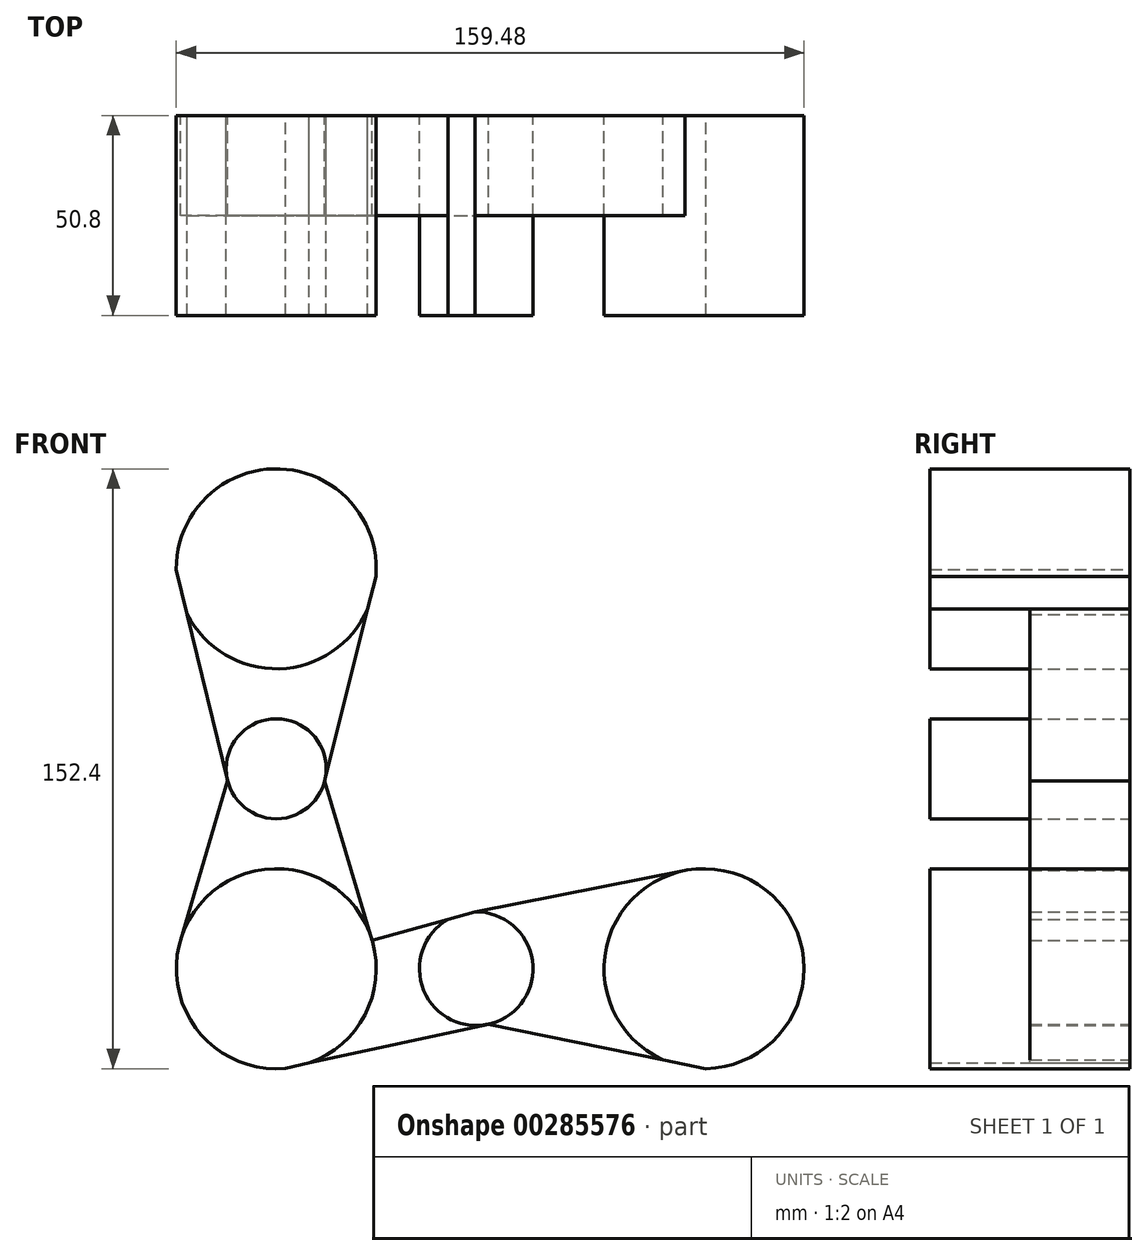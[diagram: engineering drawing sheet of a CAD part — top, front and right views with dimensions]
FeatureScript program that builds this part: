
annotation { "Feature Type Name" : "Feature", "Feature Type Description" : "" }
export const myFeature = defineFeature(function(context is Context, id is Id, definition is map)
    precondition{}
    {
        {
            var Q0;
            Q0=qCreatedBy(makeId("Front.planeOp"),FACE);
            var sketch = newSketch(context, id + "F0", { "sketchPlane" : qUnion([Q0])});
            skLineSegment(sketch, "E0", {"start": v(-135.65, -73.57) * mm, "end": v(-84.85, -73.57) * mm});
            skLineSegment(sketch, "E1", {"start": v(-77.77, -73.57) * mm, "end": v(-26.97, -73.57) * mm});
            skLineSegment(sketch, "E2", {"start": v(-135.65, -73.57) * mm, "end": v(-135.65, -22.77) * mm});
            skLineSegment(sketch, "E3", {"start": v(-135.65, -22.77) * mm, "end": v(-135.65, 28.03) * mm});
            skLineSegment(sketch, "E4", {"start": v(-77.77, -73.57) * mm, "end": v(-84.85, -73.57) * mm});
            skCircle(sketch, "E5", {"center": v(-135.65, 28.03) * mm, "radius": 25.4 * mm});
            skCircle(sketch, "E6", {"center": v(-135.65, -73.57) * mm, "radius": 25.4 * mm});
            skCircle(sketch, "E7", {"center": v(-26.97, -73.57) * mm, "radius": 25.4 * mm});
            skCircle(sketch, "E8", {"center": v(-84.85, -73.57) * mm, "radius": 14.43 * mm});
            skCircle(sketch, "E9", {"center": v(-135.65, -22.77) * mm, "radius": 12.7 * mm});
            skLineSegment(sketch, "E10", {"start": v(-161.05, 27.9) * mm, "end": v(-147.99, -25.77) * mm});
            skLineSegment(sketch, "E11", {"start": v(-147.99, -25.77) * mm, "end": v(-160, -66.36) * mm});
            skLineSegment(sketch, "E12", {"start": v(-110.32, 26.07) * mm, "end": v(-123.33, -25.85) * mm});
            skLineSegment(sketch, "E13", {"start": v(-123.33, -25.85) * mm, "end": v(-111.3, -66.33) * mm});
            skLineSegment(sketch, "E14", {"start": v(-133.3, -98.86) * mm, "end": v(-81.78, -87.67) * mm});
            skLineSegment(sketch, "E15", {"start": v(-81.78, -87.67) * mm, "end": v(-26.43, -98.96) * mm});
            skLineSegment(sketch, "E16", {"start": v(-111.3, -66.33) * mm, "end": v(-85.14, -59.14) * mm});
            skLineSegment(sketch, "E17", {"start": v(-85.14, -59.14) * mm, "end": v(-31.88, -48.65) * mm});
            skSolve(sketch);
        }
        {
            var Q0;
            {var subQ1=sQuery(id+"F0.wireOp",EDGE,"E5");var subQ4=makeQuery(id+"F0.imprint","INTERSECT",VERTEX,{"derivedFrom":[sQuery(id+"F0.wireOp",EDGE,"E3"),subQ1]});Q0=makeQuery(id+"F0.imprint","IMPRINT",FACE,{"disambiguationData":[TD([[makeQuery(id+"F0.imprint","IMPRINT",EDGE,{"disambiguationData":[TD([[subQ4,1.0]])],"derivedFrom":subQ1}),1.0]])]});}
            var Q1;
            {var subQ0=sQuery(id+"F0.wireOp",EDGE,"E3");var subQ1=sQuery(id+"F0.wireOp",EDGE,"E2");var subQ2=makeQuery(id+"F0.imprint","INTERSECT",VERTEX,{"derivedFrom":[subQ1,subQ0]});Q1=makeQuery(id+"F0.imprint","IMPRINT",FACE,{"disambiguationData":[TD([[makeQuery(id+"F0.imprint","IMPRINT",EDGE,{"disambiguationData":[TD([[subQ2,1.0]])],"derivedFrom":subQ1}),-1.0]])]});}
            var Q2;
            {var subQ0=sQuery(id+"F0.wireOp",EDGE,"E3");var subQ1=sQuery(id+"F0.wireOp",EDGE,"E2");var subQ2=makeQuery(id+"F0.imprint","INTERSECT",VERTEX,{"derivedFrom":[subQ1,subQ0]});Q2=makeQuery(id+"F0.imprint","IMPRINT",FACE,{"disambiguationData":[TD([[makeQuery(id+"F0.imprint","IMPRINT",EDGE,{"disambiguationData":[TD([[subQ2,1.0]])],"derivedFrom":subQ1}),1.0]])]});}
            var Q3;
            {var subQ5=sQuery(id+"F0.wireOp",EDGE,"E2");var subQ7=sQuery(id+"F0.wireOp",EDGE,"E0");var subQ8=makeQuery(id+"F0.imprint","INTERSECT",VERTEX,{"derivedFrom":[subQ7,subQ5]});Q3=makeQuery(id+"F0.imprint","IMPRINT",FACE,{"disambiguationData":[TD([[makeQuery(id+"F0.imprint","IMPRINT",EDGE,{"disambiguationData":[TD([[subQ8,-1.0]])],"derivedFrom":subQ7}),-1.0]])]});}
            var Q4;
            {var subQ4=sQuery(id+"F0.wireOp",EDGE,"E4");Q4=makeQuery(id+"F0.imprint","IMPRINT",FACE,{"disambiguationData":[TD([[makeQuery(id+"F0.imprint","IMPRINT",EDGE,{"derivedFrom":subQ4}),1.0]])]});}
            var Q5;
            {var subQ0=sQuery(id+"F0.wireOp",EDGE,"E7");var subQ1=makeQuery(id+"F0.imprint","INTERSECT",VERTEX,{"derivedFrom":[subQ0,sQuery(id+"F0.wireOp",EDGE,"E17")]});Q5=makeQuery(id+"F0.imprint","IMPRINT",FACE,{"disambiguationData":[TD([[makeQuery(id+"F0.imprint","IMPRINT",EDGE,{"disambiguationData":[TD([[subQ1,-1.0]])],"derivedFrom":subQ0}),1.0]])]});}
            var Q6;
            {var subQ0=sQuery(id+"F0.wireOp",EDGE,"E2");var subQ1=sQuery(id+"F0.wireOp",EDGE,"E0");var subQ2=makeQuery(id+"F0.imprint","INTERSECT",VERTEX,{"derivedFrom":[subQ1,subQ0]});Q6=makeQuery(id+"F0.imprint","IMPRINT",FACE,{"disambiguationData":[TD([[makeQuery(id+"F0.imprint","IMPRINT",EDGE,{"disambiguationData":[TD([[subQ2,-1.0]])],"derivedFrom":subQ1}),1.0]])]});}
            var Q7;
            {var subQ5=sQuery(id+"F0.wireOp",EDGE,"E4");Q7=makeQuery(id+"F0.imprint","IMPRINT",FACE,{"disambiguationData":[TD([[makeQuery(id+"F0.imprint","IMPRINT",EDGE,{"derivedFrom":subQ5}),-1.0]])]});}
            extrude(context, id + "F1", {"entities" : qUnion([Q0, Q1, Q2, Q3, Q4, Q5, Q6, Q7]), "depth" : 50.8 * mm});
        }
        {
            var Q0;
            {var subQ0=sQuery(id+"F0.wireOp",EDGE,"E5");var subQ1=sQuery(id+"F0.wireOp",EDGE,"E3");var subQ2=makeQuery(id+"F0.imprint","INTERSECT",VERTEX,{"derivedFrom":[subQ1,subQ0]});Q0=makeQuery(id+"F0.imprint","IMPRINT",FACE,{"disambiguationData":[TD([[makeQuery(id+"F0.imprint","IMPRINT",EDGE,{"disambiguationData":[TD([[subQ2,1.0]])],"derivedFrom":subQ1}),1.0]])]});}
            var Q1;
            {var subQ0=sQuery(id+"F0.wireOp",EDGE,"E5");var subQ1=sQuery(id+"F0.wireOp",EDGE,"E3");var subQ2=makeQuery(id+"F0.imprint","INTERSECT",VERTEX,{"derivedFrom":[subQ1,subQ0]});Q1=makeQuery(id+"F0.imprint","IMPRINT",FACE,{"disambiguationData":[TD([[makeQuery(id+"F0.imprint","IMPRINT",EDGE,{"disambiguationData":[TD([[subQ2,1.0]])],"derivedFrom":subQ1}),-1.0]])]});}
            var Q2;
            {var subQ5=sQuery(id+"F0.wireOp",EDGE,"E13");Q2=makeQuery(id+"F0.imprint","IMPRINT",FACE,{"disambiguationData":[TD([[makeQuery(id+"F0.imprint","IMPRINT",EDGE,{"derivedFrom":subQ5}),-1.0]])]});}
            var Q3;
            {var subQ5=sQuery(id+"F0.wireOp",EDGE,"E11");Q3=makeQuery(id+"F0.imprint","IMPRINT",FACE,{"disambiguationData":[TD([[makeQuery(id+"F0.imprint","IMPRINT",EDGE,{"derivedFrom":subQ5}),1.0]])]});}
            var Q4;
            {var subQ5=sQuery(id+"F0.wireOp",EDGE,"E17");Q4=makeQuery(id+"F0.imprint","IMPRINT",FACE,{"disambiguationData":[TD([[makeQuery(id+"F0.imprint","IMPRINT",EDGE,{"derivedFrom":subQ5}),-1.0]])]});}
            var Q5;
            {var subQ0=sQuery(id+"F0.wireOp",EDGE,"E7");var subQ1=sQuery(id+"F0.wireOp",EDGE,"E1");var subQ2=makeQuery(id+"F0.imprint","INTERSECT",VERTEX,{"derivedFrom":[subQ1,subQ0]});Q5=makeQuery(id+"F0.imprint","IMPRINT",FACE,{"disambiguationData":[TD([[makeQuery(id+"F0.imprint","IMPRINT",EDGE,{"disambiguationData":[TD([[subQ2,1.0]])],"derivedFrom":subQ1}),-1.0]])]});}
            extrude(context, id + "F2", {"entities" : qUnion([Q0, Q1, Q2, Q3, Q4, Q5]), "depth" : 25.4 * mm});
        }
        {
            var Q0;
            {var subQ0=sQuery(id+"F0.wireOp",EDGE,"E6");var subQ1=sQuery(id+"F0.wireOp",EDGE,"E0");var subQ2=makeQuery(id+"F0.imprint","INTERSECT",VERTEX,{"derivedFrom":[subQ1,subQ0]});Q0=makeQuery(id+"F0.imprint","IMPRINT",FACE,{"disambiguationData":[TD([[makeQuery(id+"F0.imprint","IMPRINT",EDGE,{"disambiguationData":[TD([[subQ2,-1.0]])],"derivedFrom":subQ1}),1.0]])]});}
            var Q1;
            {var subQ0=sQuery(id+"F0.wireOp",EDGE,"E6");var subQ1=sQuery(id+"F0.wireOp",EDGE,"E0");var subQ2=makeQuery(id+"F0.imprint","INTERSECT",VERTEX,{"derivedFrom":[subQ1,subQ0]});Q1=makeQuery(id+"F0.imprint","IMPRINT",FACE,{"disambiguationData":[TD([[makeQuery(id+"F0.imprint","IMPRINT",EDGE,{"disambiguationData":[TD([[subQ2,-1.0]])],"derivedFrom":subQ1}),-1.0]])]});}
            extrude(context, id + "F3", {"entities" : qUnion([Q0, Q1]), "depth" : 25.4 * mm});
        }
    });
